# Revit family: Accessory-Grab_Bar-KOHLER-K-33676T_1
name_source: partatom
category: Specialty Equipment
units: mm (PartAtom-declared; Revit-internal decimal feet)

## family parameters
Cut with Voids When Loaded = No
Host = Face
OmniClass Number = 23.31.25.00
OmniClass Title = Toilet and Bath Specialties
Part Type = Normal
Room Calculation Point = No
Round Connector Dimension = Use Diameter
Shared = No

## types (4) — shared parameters
ADA Compliant = No
Assembly Code = C1030200
Date Modified = 3/16/2024
Default Elevation = 42"
Description = 12 Inch Grab Bar
Height = 1 3/4"
Length = 14 3/4"
Manufacturer = Kohler Co.
Master Format 2014 = 10 28 00
Master Format 2014 Name = Toilet, Bath, and Laundry Accessories
Material = Premium Metal construction
URL = http://www.kohler.com.cn
WaterSense Certified = No
Width = 3 1/8"

## per-type parameters (varying)
| type | Finish | Model | Type |
| BL-Matte Black | Kohler-Metal-BL-Matte_Black | K-33676T-BL | 2 |
| CP-Polished Chrome | Kohler-Metal-CP-Polished_Chrome | K-33676T-CP | 1 |
| 2MB-Vibrant Brushed Moderne Brass | Kohler-Metal-2MB-Vibrant_Brushed_Moderne_Brass | K-33676T-2MB | 3 |
| BN-Vibrant Brushed Nickel | Kohler-Metal-BN-Vibrant_Brushed_Nickel | K-33676T-BN | 4 |

## geometry (parser evidence)
native form markers: Sweep x5
no freeform markers — native parametric forms only
